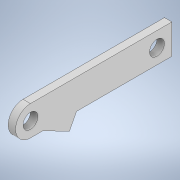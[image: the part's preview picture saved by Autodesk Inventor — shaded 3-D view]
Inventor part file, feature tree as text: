
AUTODESK INVENTOR PART (.ipt)
format: ipt  version: 2021 (Build 250183000, 183)  size: 134,656 bytes
history: native  units: in
note: dims shown in document units (in); Inventor stores cm internally (conversion verified against a paired STEP export)
features: extrude x4, sketch x4, projected_geometry x1
ambient origin geometry x8: Origin, YZ Plane, XZ Plane, XY Plane, X Axis, Y Axis, Z Axis, Center Point
bodies: Solid1 (feature_tree)
feature tree (9):
  extrude  "Extrusion1"  Depth=5.25in
  extrude  "Extrusion2"  Depth=1.0in
  extrude  "Extrusion3"  Depth=0.5in
  extrude  "Extrusion4"  Depth=5.25in
  sketch  "Sketch1"  dims[d0=1.0in d1=5.25in]
  sketch  "Sketch2"  dims[d2=0.25in d3=0.0in d4=1.0in]
  projected_geometry  "Projected Loop1"
  sketch  "Sketch3"  dims[d5=0.5in d6=0.5in]
  sketch  "Sketch4"  dims[d7=4.25in d8=5.25in d9=0.5in d10=0.5in d11=0.5in d12=0.25in d13=0.0in d14=0.25in d15=0.0in d16=0.1886in d19=1.0in d20=0.25in d21=0.0in]
